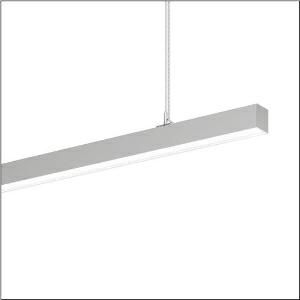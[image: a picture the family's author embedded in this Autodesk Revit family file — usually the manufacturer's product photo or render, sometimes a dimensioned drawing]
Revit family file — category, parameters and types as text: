
# Revit family: silica_r__21_51mx33tat7s_6391
name_source: partatom
category: Lighting Fixtures
units: mm (PartAtom-declared; Revit-internal decimal feet)

## family parameters
Cut with Voids When Loaded = No
Host = Face
Light Source = No
Part Type = Normal
Room Calculation Point = No
Round Connector Dimension = Use Diameter
Shared = No

## types (1)
- --- (1 x LED, 5740 lm, 53.8 W, 6500K)
    Apparent Load = 54 VA
    CIE Flux Codes = 78 96 99 56 100
    Color Rendering = 80
    Color Temperature = 6500K
    Default Elevation = 1800 mm
    Description = Silica® 21, office luminaire, primary optical cover: prismatic diffuser, of PMMA, CAT 2 (L<= 3000cd/m²), light emission: direct/indirect distribution, primary light characteristic: symmetric, installation type: suspended mounting, LED, rated luminous flux: 5.740lm, luminous efficacy: 102lm/W, light colour: 8tw, colour temperature: 2700..6500K, control gear: ECG DALI, with terminal, 3+2-pole, max. 2.5mm², mains connection: 220..240V, AC, 50/60Hz, rated input power: 56.5W, luminaire housing, of aluminium, metallic grey (RAL 9006), length: 1.204mm, width: 53mm, height: 53mm, protection rating (complete): IP20, insulation class (complete): insulation class I (protective earthing), certification: CE, permissible operating ambient temperature: 0..+35°C, standard: EN 50419, packaging unit: 1 piece
    Height = 53 mm
    Lamp = 1 x LED
    Lamp Light Flux = 5740 lm
    Lamp Power = 53.8 W
    Lamp count = 1
    Length = 1204 mm
    Luminous efficacy = 107 lm/W
    Manufacturer = Siteco
    ModVariant = No
    Model = 51MX33TAT7S
    Mounting Place = Ceiling
    Mounting Type = Pendant
    Number of Poles = 1
    OnlyDefault = Yes
    Power Factor = 1
    Product Name = Silica® 21
    Product group = office luminaire | ceiling pendant
    ProductGroupID = 902
    Protection Class = Protection class I
    Protection Degree = IP 20
    RLX_Detail_Level = 1
    RLX_Emergency_Light_Flux = 0 lm
    RLX_Emergency_Type = 0
    RLX_Emergency_Type_DB = No
    RlxData = <blob elided: 20225 chars, md5=f34ce262>
    Socket = socket
    Standby Power = 0 W
    System Light Flux = 5740 lm
    System Power = 54 W
    Type Comments = individual setting
    Type Image = l_1297747.jpg
    URL = http://relux.com
    VarID = @adj_071071
    Voltage = 0 V
    Weight = 0.00 kg
    Width = 53 mm

## geometry (parser evidence)
native form markers: Blend x4, Sweep x11
no freeform markers — native parametric forms only
